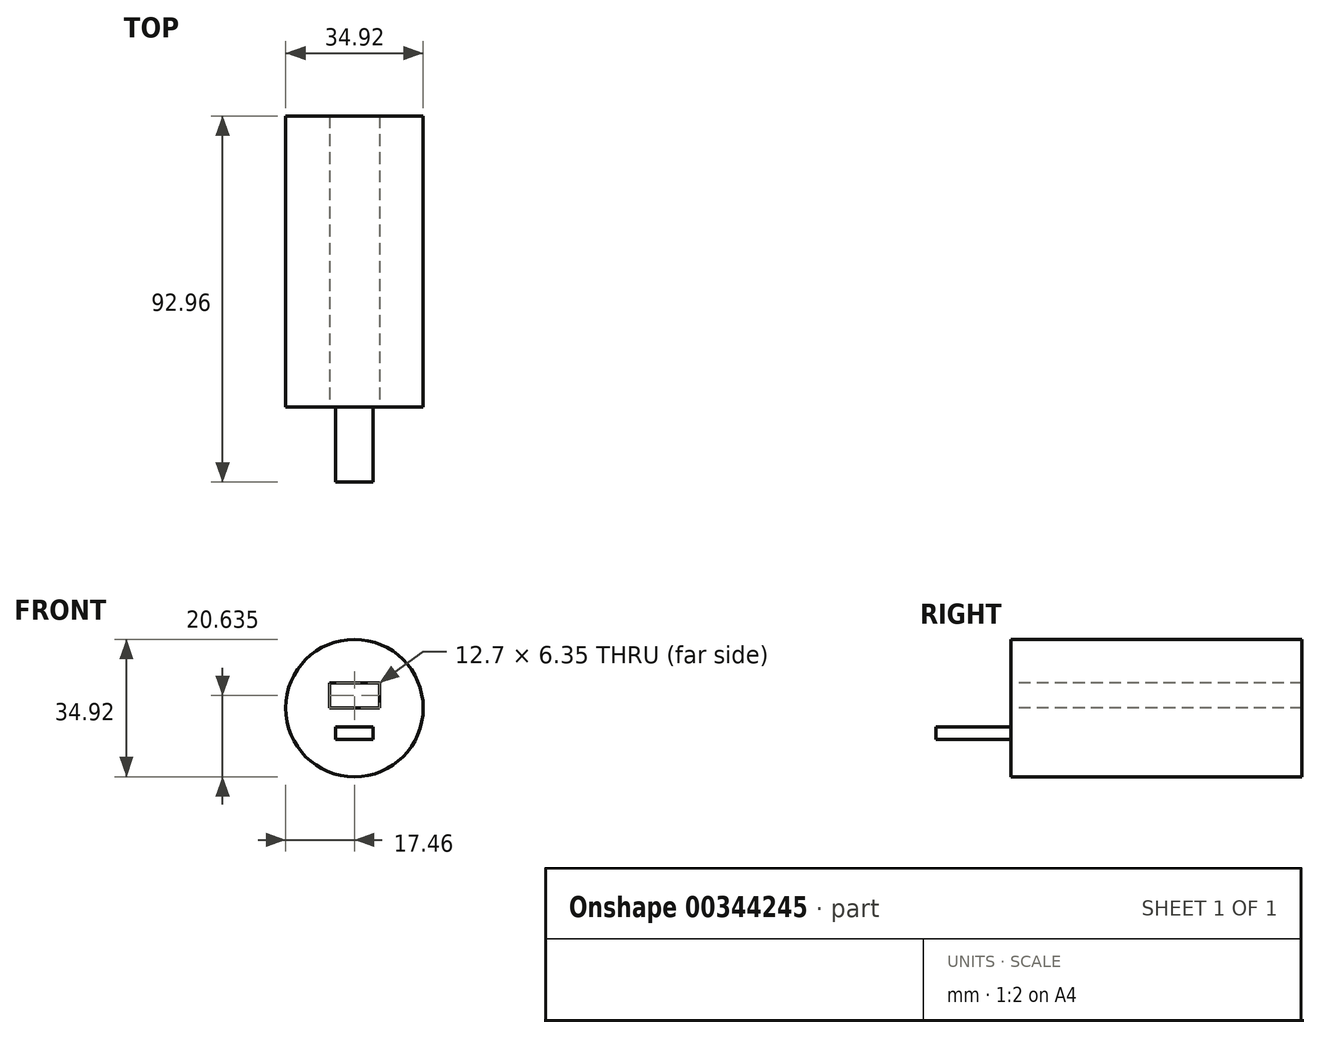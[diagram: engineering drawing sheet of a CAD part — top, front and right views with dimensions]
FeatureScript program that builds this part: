
annotation { "Feature Type Name" : "Feature", "Feature Type Description" : "" }
export const myFeature = defineFeature(function(context is Context, id is Id, definition is map)
    precondition{}
    {
        {
            var Q0;
            Q0=qCreatedBy(makeId("Front.planeOp"),FACE);
            var sketch = newSketch(context, id + "F0", { "sketchPlane" : qUnion([Q0])});
            skCircle(sketch, "E0", {"center": v(0, 0) * mm, "radius": 17.46 * mm});
            skSolve(sketch);
        }
        {
            var Q0;
            Q0=makeQuery(id+"F0.imprint","IMPRINT",FACE,{"disambiguationData":[TD([[makeQuery(id+"F0.imprint","IMPRINT",EDGE,{"derivedFrom":sQuery(id+"F0.wireOp",EDGE,"E0")}),1.0]])]});
            extrude(context, id + "F1", {"entities" : qUnion([Q0]), "depth" : 73.9 * mm});
        }
        {
            var Q0;
            Q0=makeQuery(id+"F1.opExtrude","CAP_FACE",FACE,{"disambiguationData":[OSD([sQuery(id+"F0.wireOp",EDGE,"E0")])],"isStart":false});
            var sketch = newSketch(context, id + "F2", { "sketchPlane" : qUnion([Q0])});
            skLineSegment(sketch, "E1.bottom", {"start": v(-6.35, 6.35) * mm, "end": v(6.35, 6.35) * mm});
            skLineSegment(sketch, "E1.top", {"start": v(-6.35, 0) * mm, "end": v(6.35, 0) * mm});
            skLineSegment(sketch, "E1.left", {"start": v(-6.35, 6.35) * mm, "end": v(-6.35, 0) * mm});
            skLineSegment(sketch, "E1.right", {"start": v(6.35, 6.35) * mm, "end": v(6.35, 0) * mm});
            skSolve(sketch);
        }
        {
            var Q0;
            Q0=makeQuery(id+"F2.imprint","IMPRINT",FACE,{"disambiguationData":[TD([[makeQuery(id+"F2.imprint","IMPRINT",EDGE,{"derivedFrom":sQuery(id+"F2.wireOp",EDGE,"E1.bottom")}),-1.0]])]});
            extrude(context, id + "F3", {"entities" : qUnion([Q0]), "operationType" : NewBodyOperationType.REMOVE, "oppositeDirection" : true, "depth" : 178.05 * mm});
        }
        {
            var Q0;
            Q0=makeQuery(id+"F1.opExtrude","CAP_FACE",FACE,{"disambiguationData":[OSD([sQuery(id+"F0.wireOp",EDGE,"E0")])],"isStart":false});
            var sketch = newSketch(context, id + "F4", { "sketchPlane" : qUnion([Q0])});
            skLineSegment(sketch, "E2.bottom", {"start": v(4.76, -4.76) * mm, "end": v(-4.76, -4.76) * mm});
            skLineSegment(sketch, "E2.top", {"start": v(4.76, -7.94) * mm, "end": v(-4.76, -7.94) * mm});
            skLineSegment(sketch, "E2.left", {"start": v(-4.76, -7.94) * mm, "end": v(-4.76, -4.76) * mm});
            skLineSegment(sketch, "E2.right", {"start": v(4.76, -7.94) * mm, "end": v(4.76, -4.76) * mm});
            skPoint(sketch, "E3", {"position": v(0, -4.76) * mm});
            skSolve(sketch);
        }
        {
            var Q0;
            Q0=makeQuery(id+"F4.imprint","IMPRINT",FACE,{"disambiguationData":[TD([[makeQuery(id+"F4.imprint","IMPRINT",EDGE,{"derivedFrom":sQuery(id+"F4.wireOp",EDGE,"E2.bottom")}),1.0]])]});
            extrude(context, id + "F5", {"entities" : qUnion([Q0]), "operationType" : NewBodyOperationType.ADD, "depth" : 19.05 * mm});
        }
    });
